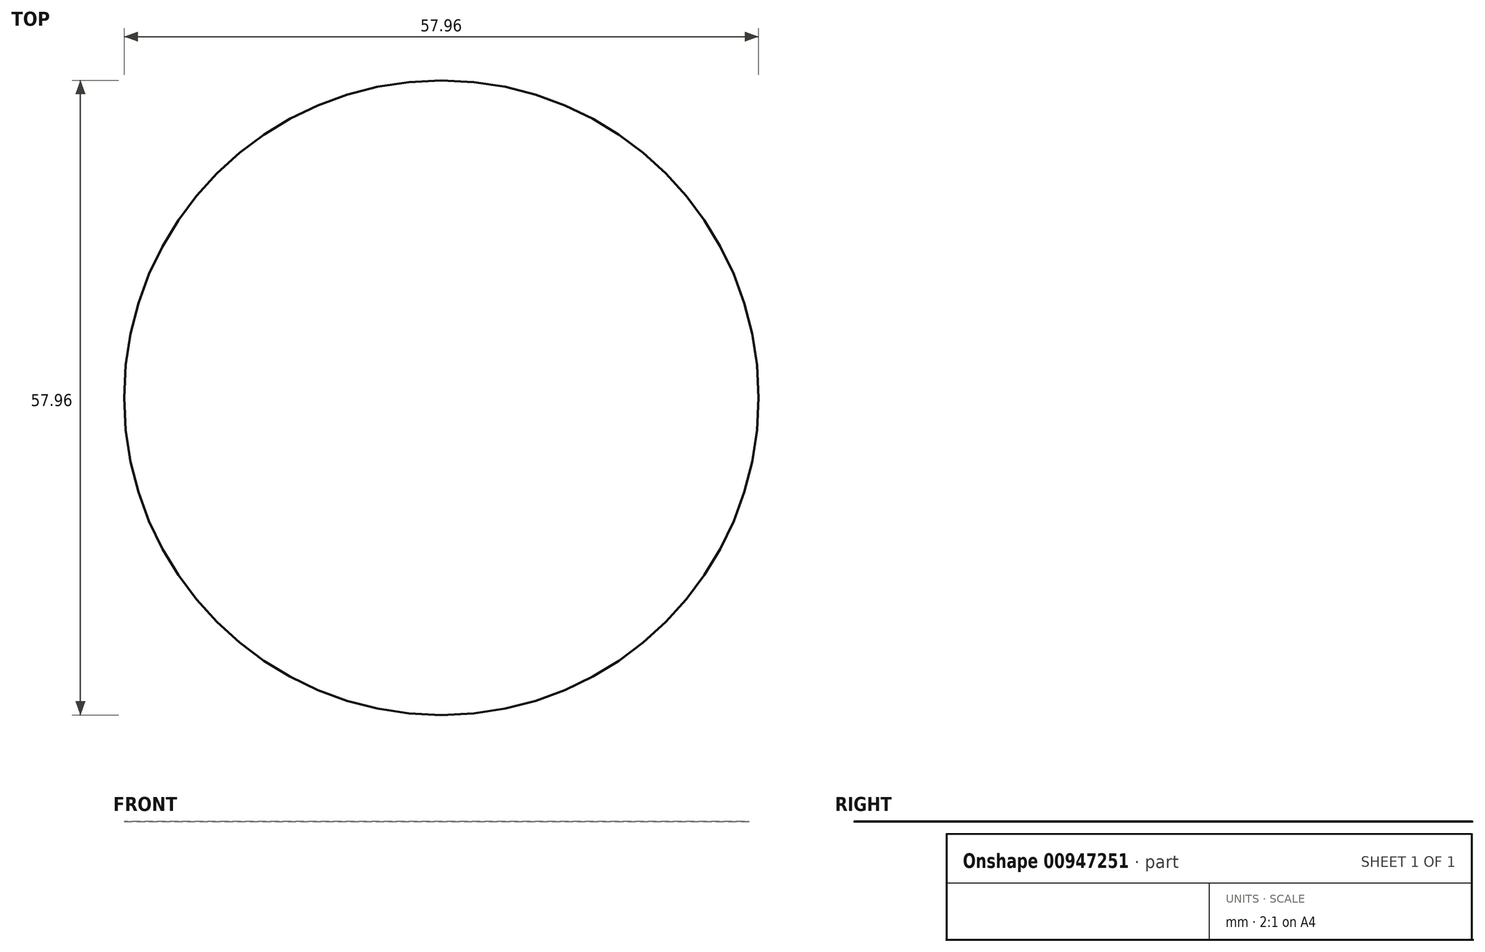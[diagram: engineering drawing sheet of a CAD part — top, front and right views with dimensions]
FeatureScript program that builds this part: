
annotation { "Feature Type Name" : "Feature", "Feature Type Description" : "" }
export const myFeature = defineFeature(function(context is Context, id is Id, definition is map)
    precondition{}
    {
        {
            var Q0;
            Q0=qCreatedBy(makeId("Front.planeOp"),FACE);
            var sketch = newSketch(context, id + "F0", { "sketchPlane" : qUnion([Q0])});
            skLineSegment(sketch, "E0", {"start": v(0, 0) * mm, "end": v(0, 62.66) * mm});
            skLineSegment(sketch, "E1", {"start": v(0, 62.66) * mm, "end": v(28.98, 62.66) * mm});
            skArc(sketch, "E2", {"start": v(28.98, 62.66) * mm, "mid": v(7.6, 34.52) * mm, "end": v(0, 0) * mm});
            skSolve(sketch);
        }
        {
            var Q0;
            Q0=makeQuery(id+"F0.imprint","IMPRINT",FACE,{"disambiguationData":[TD([[makeQuery(id+"F0.imprint","IMPRINT",EDGE,{"derivedFrom":sQuery(id+"F0.wireOp",EDGE,"E0")}),-1.0]])]});
            var Q1;
            Q1=sQuery(id+"F0.wireOp",EDGE,"E0");
            revolve(context, id + "F1", {"surfaceOperationType" : NewSurfaceOperationType.NEW, "entities" : qUnion([Q0]), "axis" : qUnion([Q1]), "revolveType" : RevolveType.FULL});
        }
    });
